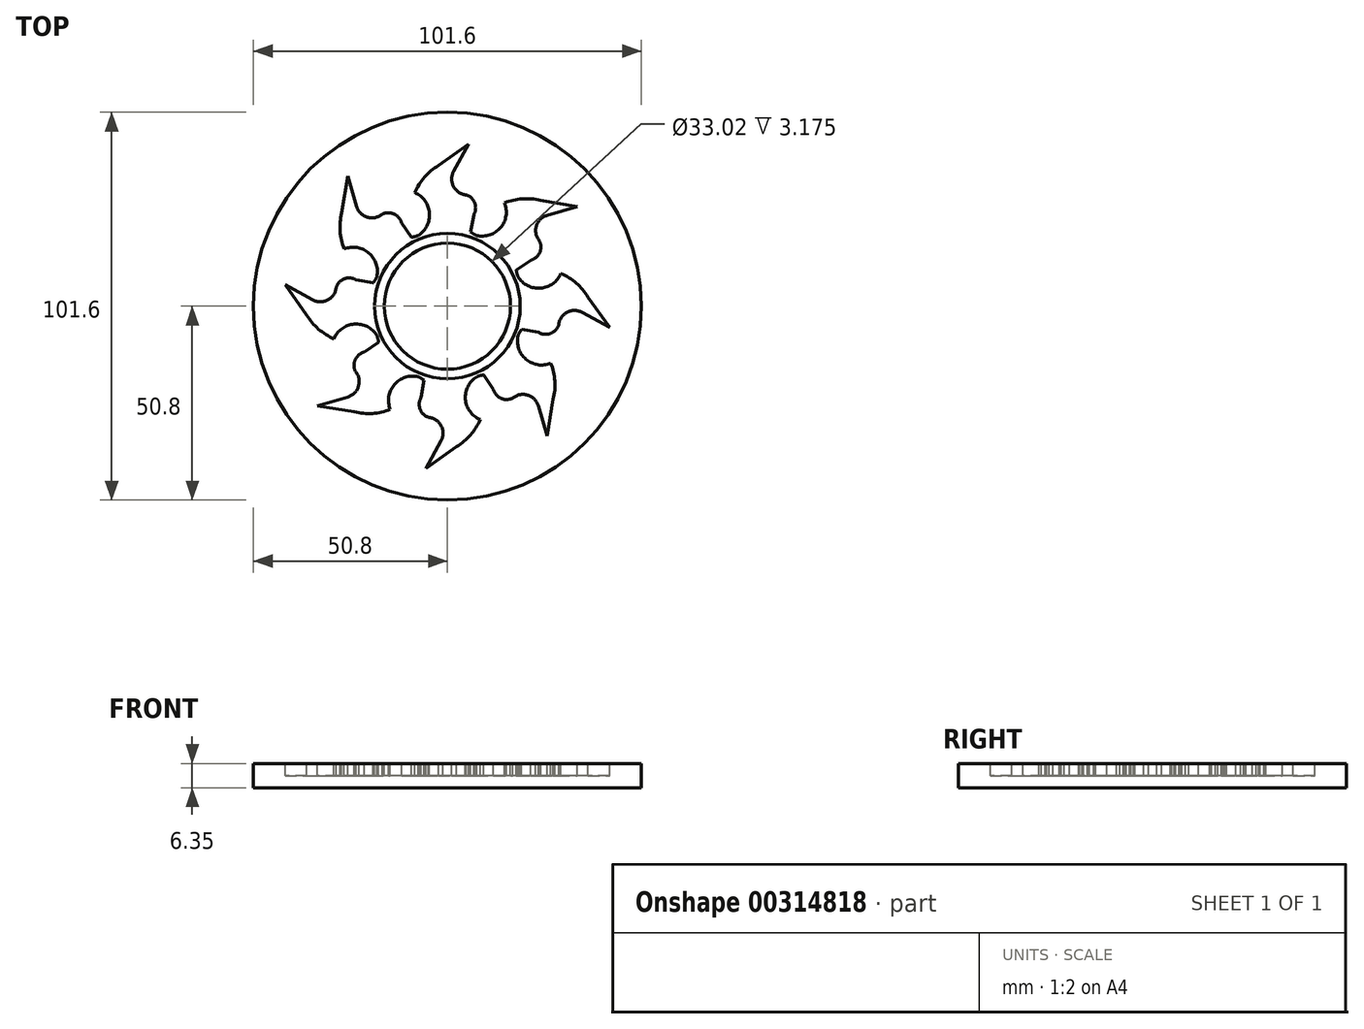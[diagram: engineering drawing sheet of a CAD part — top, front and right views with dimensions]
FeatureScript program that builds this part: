
annotation { "Feature Type Name" : "Feature", "Feature Type Description" : "" }
export const myFeature = defineFeature(function(context is Context, id is Id, definition is map)
    precondition{}
    {
        {
            var Q0;
            Q0=qCreatedBy(makeId("Top.planeOp"),FACE);
            var sketch = newSketch(context, id + "F0", { "sketchPlane" : qUnion([Q0])});
            skCircle(sketch, "E0", {"center": v(0, 0) * mm, "radius": 50.8 * mm});
            skSolve(sketch);
        }
        {
            var Q0;
            Q0 = qSketchRegion(id + "F0", true);
            extrude(context, id + "F1", {"entities" : qUnion([Q0]), "depth" : 6.35 * mm});
        }
        {
            var Q0;
            Q0=makeQuery(id+"F1.opExtrude","CAP_FACE",FACE,{"disambiguationData":[OSD([sQuery(id+"F0.wireOp",EDGE,"E0")])],"isStart":false});
            var sketch = newSketch(context, id + "F2", { "sketchPlane" : qUnion([Q0])});
            skCircle(sketch, "E1", {"center": v(0, 0) * mm, "radius": 16.51 * mm});
            skCircle(sketch, "E2", {"center": v(0, 0) * mm, "radius": 19.05 * mm});
            skLineSegment(sketch, "E3", {"start": v(0, 0) * mm, "end": v(-55.8, 0) * mm, "construction": true});
            skArc(sketch, "E4", {"start": v(-18.5, 7.66) * mm, "mid": v(-20.57, 13.92) * mm, "end": v(-27.06, 14.97) * mm});
            skArc(sketch, "E5", {"start": v(-27.7, 24.38) * mm, "mid": v(-28.12, 19.62) * mm, "end": v(-27.06, 14.97) * mm});
            skArc(sketch, "E6", {"start": v(-19.42, 6.08) * mm, "mid": v(-18.91, 6.84) * mm, "end": v(-18.5, 7.66) * mm});
            skArc(sketch, "E7", {"start": v(-23.8, 26.1) * mm, "mid": v(-20.98, 23.29) * mm, "end": v(-17.09, 24.1) * mm});
            skArc(sketch, "E8", {"start": v(-12.01, 21.75) * mm, "mid": v(-13.99, 24.14) * mm, "end": v(-17.09, 24.1) * mm});
            skLineSegment(sketch, "E9", {"start": v(-27.7, 24.38) * mm, "end": v(-26.09, 34.02) * mm});
            skLineSegment(sketch, "E10", {"start": v(-26.09, 34.02) * mm, "end": v(-23.8, 26.1) * mm});
            skLineSegment(sketch, "E11", {"start": v(-12.01, 21.75) * mm, "end": v(-9.43, 18.03) * mm});
            skArc(sketch, "E12.1.0", {"start": v(-36.83, -2.35) * mm, "mid": v(-33.76, -6.01) * mm, "end": v(-29.72, -8.56) * mm});
            skLineSegment(sketch, "E12.1.1", {"start": v(-23.88, 6.89) * mm, "end": v(-19.42, 6.08) * mm});
            skLineSegment(sketch, "E12.1.2", {"start": v(-36.83, -2.35) * mm, "end": v(-42.5, 5.6) * mm});
            skLineSegment(sketch, "E12.1.3", {"start": v(-42.5, 5.6) * mm, "end": v(-35.28, 1.63) * mm});
            skArc(sketch, "E12.1.4", {"start": v(-35.28, 1.63) * mm, "mid": v(-31.3, 1.63) * mm, "end": v(-29.13, 4.97) * mm});
            skArc(sketch, "E12.1.5", {"start": v(-23.88, 6.89) * mm, "mid": v(-26.96, 7.18) * mm, "end": v(-29.13, 4.97) * mm});
            skArc(sketch, "E12.1.6", {"start": v(-18.5, -7.66) * mm, "mid": v(-24.38, -4.7) * mm, "end": v(-29.72, -8.56) * mm});
            skArc(sketch, "E12.1.7", {"start": v(-18.03, -9.43) * mm, "mid": v(-18.21, -8.53) * mm, "end": v(-18.5, -7.66) * mm});
            skArc(sketch, "E12.2.0", {"start": v(-24.38, -27.7) * mm, "mid": v(-19.62, -28.12) * mm, "end": v(-14.97, -27.06) * mm});
            skLineSegment(sketch, "E12.2.1", {"start": v(-21.75, -12.01) * mm, "end": v(-18.03, -9.43) * mm});
            skLineSegment(sketch, "E12.2.2", {"start": v(-24.38, -27.7) * mm, "end": v(-34.02, -26.09) * mm});
            skLineSegment(sketch, "E12.2.3", {"start": v(-34.02, -26.09) * mm, "end": v(-26.1, -23.8) * mm});
            skArc(sketch, "E12.2.4", {"start": v(-26.1, -23.8) * mm, "mid": v(-23.29, -20.98) * mm, "end": v(-24.1, -17.09) * mm});
            skArc(sketch, "E12.2.5", {"start": v(-21.75, -12.01) * mm, "mid": v(-24.14, -13.99) * mm, "end": v(-24.1, -17.09) * mm});
            skArc(sketch, "E12.2.6", {"start": v(-7.66, -18.5) * mm, "mid": v(-13.92, -20.57) * mm, "end": v(-14.97, -27.06) * mm});
            skArc(sketch, "E12.2.7", {"start": v(-6.08, -19.42) * mm, "mid": v(-6.84, -18.91) * mm, "end": v(-7.66, -18.5) * mm});
            skArc(sketch, "E12.3.0", {"start": v(2.35, -36.83) * mm, "mid": v(6.01, -33.76) * mm, "end": v(8.56, -29.72) * mm});
            skLineSegment(sketch, "E12.3.1", {"start": v(-6.89, -23.88) * mm, "end": v(-6.08, -19.42) * mm});
            skLineSegment(sketch, "E12.3.2", {"start": v(2.35, -36.83) * mm, "end": v(-5.6, -42.5) * mm});
            skLineSegment(sketch, "E12.3.3", {"start": v(-5.6, -42.5) * mm, "end": v(-1.63, -35.28) * mm});
            skArc(sketch, "E12.3.4", {"start": v(-1.63, -35.28) * mm, "mid": v(-1.63, -31.3) * mm, "end": v(-4.97, -29.13) * mm});
            skArc(sketch, "E12.3.5", {"start": v(-6.89, -23.88) * mm, "mid": v(-7.18, -26.96) * mm, "end": v(-4.97, -29.13) * mm});
            skArc(sketch, "E12.3.6", {"start": v(7.66, -18.5) * mm, "mid": v(4.7, -24.38) * mm, "end": v(8.56, -29.72) * mm});
            skArc(sketch, "E12.3.7", {"start": v(9.43, -18.03) * mm, "mid": v(8.53, -18.21) * mm, "end": v(7.66, -18.5) * mm});
            skArc(sketch, "E12.4.0", {"start": v(27.7, -24.38) * mm, "mid": v(28.12, -19.62) * mm, "end": v(27.06, -14.97) * mm});
            skLineSegment(sketch, "E12.4.1", {"start": v(12.01, -21.75) * mm, "end": v(9.43, -18.03) * mm});
            skLineSegment(sketch, "E12.4.2", {"start": v(27.7, -24.38) * mm, "end": v(26.09, -34.02) * mm});
            skLineSegment(sketch, "E12.4.3", {"start": v(26.09, -34.02) * mm, "end": v(23.8, -26.1) * mm});
            skArc(sketch, "E12.4.4", {"start": v(23.8, -26.1) * mm, "mid": v(20.98, -23.29) * mm, "end": v(17.09, -24.1) * mm});
            skArc(sketch, "E12.4.5", {"start": v(12.01, -21.75) * mm, "mid": v(13.99, -24.14) * mm, "end": v(17.09, -24.1) * mm});
            skArc(sketch, "E12.4.6", {"start": v(18.5, -7.66) * mm, "mid": v(20.57, -13.92) * mm, "end": v(27.06, -14.97) * mm});
            skArc(sketch, "E12.4.7", {"start": v(19.42, -6.08) * mm, "mid": v(18.91, -6.84) * mm, "end": v(18.5, -7.66) * mm});
            skArc(sketch, "E12.5.0", {"start": v(36.83, 2.35) * mm, "mid": v(33.76, 6.01) * mm, "end": v(29.72, 8.56) * mm});
            skLineSegment(sketch, "E12.5.1", {"start": v(23.88, -6.89) * mm, "end": v(19.42, -6.08) * mm});
            skLineSegment(sketch, "E12.5.2", {"start": v(36.83, 2.35) * mm, "end": v(42.5, -5.6) * mm});
            skLineSegment(sketch, "E12.5.3", {"start": v(42.5, -5.6) * mm, "end": v(35.28, -1.63) * mm});
            skArc(sketch, "E12.5.4", {"start": v(35.28, -1.63) * mm, "mid": v(31.3, -1.63) * mm, "end": v(29.13, -4.97) * mm});
            skArc(sketch, "E12.5.5", {"start": v(23.88, -6.89) * mm, "mid": v(26.96, -7.18) * mm, "end": v(29.13, -4.97) * mm});
            skArc(sketch, "E12.5.6", {"start": v(18.5, 7.66) * mm, "mid": v(24.38, 4.7) * mm, "end": v(29.72, 8.56) * mm});
            skArc(sketch, "E12.5.7", {"start": v(18.03, 9.43) * mm, "mid": v(18.21, 8.53) * mm, "end": v(18.5, 7.66) * mm});
            skArc(sketch, "E12.6.0", {"start": v(24.38, 27.7) * mm, "mid": v(19.62, 28.12) * mm, "end": v(14.97, 27.06) * mm});
            skLineSegment(sketch, "E12.6.1", {"start": v(21.75, 12.01) * mm, "end": v(18.03, 9.43) * mm});
            skLineSegment(sketch, "E12.6.2", {"start": v(24.38, 27.7) * mm, "end": v(34.02, 26.09) * mm});
            skLineSegment(sketch, "E12.6.3", {"start": v(34.02, 26.09) * mm, "end": v(26.1, 23.8) * mm});
            skArc(sketch, "E12.6.4", {"start": v(26.1, 23.8) * mm, "mid": v(23.29, 20.98) * mm, "end": v(24.1, 17.09) * mm});
            skArc(sketch, "E12.6.5", {"start": v(21.75, 12.01) * mm, "mid": v(24.14, 13.99) * mm, "end": v(24.1, 17.09) * mm});
            skArc(sketch, "E12.6.6", {"start": v(7.66, 18.5) * mm, "mid": v(13.92, 20.57) * mm, "end": v(14.97, 27.06) * mm});
            skArc(sketch, "E12.6.7", {"start": v(6.08, 19.42) * mm, "mid": v(6.84, 18.91) * mm, "end": v(7.66, 18.5) * mm});
            skArc(sketch, "E12.7.0", {"start": v(-2.35, 36.83) * mm, "mid": v(-6.01, 33.76) * mm, "end": v(-8.56, 29.72) * mm});
            skLineSegment(sketch, "E12.7.1", {"start": v(6.89, 23.88) * mm, "end": v(6.08, 19.42) * mm});
            skLineSegment(sketch, "E12.7.2", {"start": v(-2.35, 36.83) * mm, "end": v(5.6, 42.5) * mm});
            skLineSegment(sketch, "E12.7.3", {"start": v(5.6, 42.5) * mm, "end": v(1.63, 35.28) * mm});
            skArc(sketch, "E12.7.4", {"start": v(1.63, 35.28) * mm, "mid": v(1.63, 31.3) * mm, "end": v(4.97, 29.13) * mm});
            skArc(sketch, "E12.7.5", {"start": v(6.89, 23.88) * mm, "mid": v(7.18, 26.96) * mm, "end": v(4.97, 29.13) * mm});
            skArc(sketch, "E12.7.6", {"start": v(-7.66, 18.5) * mm, "mid": v(-4.7, 24.38) * mm, "end": v(-8.56, 29.72) * mm});
            skArc(sketch, "E12.7.7", {"start": v(-9.43, 18.03) * mm, "mid": v(-8.53, 18.21) * mm, "end": v(-7.66, 18.5) * mm});
            skPoint(sketch, "E13.orphan", {"position": v(-20.12, 6.2) * mm});
            skPoint(sketch, "E14.orphan", {"position": v(-9.84, 18.61) * mm});
            skPoint(sketch, "E15.orphan", {"position": v(6.2, 20.12) * mm});
            skPoint(sketch, "E16.orphan", {"position": v(18.61, 9.84) * mm});
            skPoint(sketch, "E17.orphan", {"position": v(20.12, -6.2) * mm});
            skPoint(sketch, "E18.orphan", {"position": v(9.84, -18.61) * mm});
            skPoint(sketch, "E19.orphan", {"position": v(-6.2, -20.12) * mm});
            skPoint(sketch, "E20.orphan", {"position": v(-18.61, -9.84) * mm});
            skPoint(sketch, "E21.orphan", {"position": v(-17.98, -10.9) * mm});
            skPoint(sketch, "E22.orphan", {"position": v(-5, -20.42) * mm});
            skPoint(sketch, "E23.orphan", {"position": v(10.9, -17.98) * mm});
            skPoint(sketch, "E24.orphan", {"position": v(20.42, -5) * mm});
            skPoint(sketch, "E25.orphan", {"position": v(17.98, 10.9) * mm});
            skPoint(sketch, "E26.orphan", {"position": v(5, 20.42) * mm});
            skPoint(sketch, "E27.orphan", {"position": v(-10.9, 17.98) * mm});
            skPoint(sketch, "E28.orphan", {"position": v(-20.42, 5) * mm});
            skSolve(sketch);
        }
        {
            var Q0;
            Q0 = qSketchRegion(id + "F2", true);
            var Q1;
            Q1=makeQuery(id+"F2.imprint","IMPRINT",FACE,{"disambiguationData":[TD([[makeQuery(id+"F2.imprint","IMPRINT",EDGE,{"derivedFrom":sQuery(id+"F2.wireOp",EDGE,"E1")}),1.0]])]});
            extrude(context, id + "F3", {"entities" : qUnion([Q0, Q1]), "operationType" : NewBodyOperationType.REMOVE, "oppositeDirection" : true, "depth" : 3.17 * mm});
        }
    });
